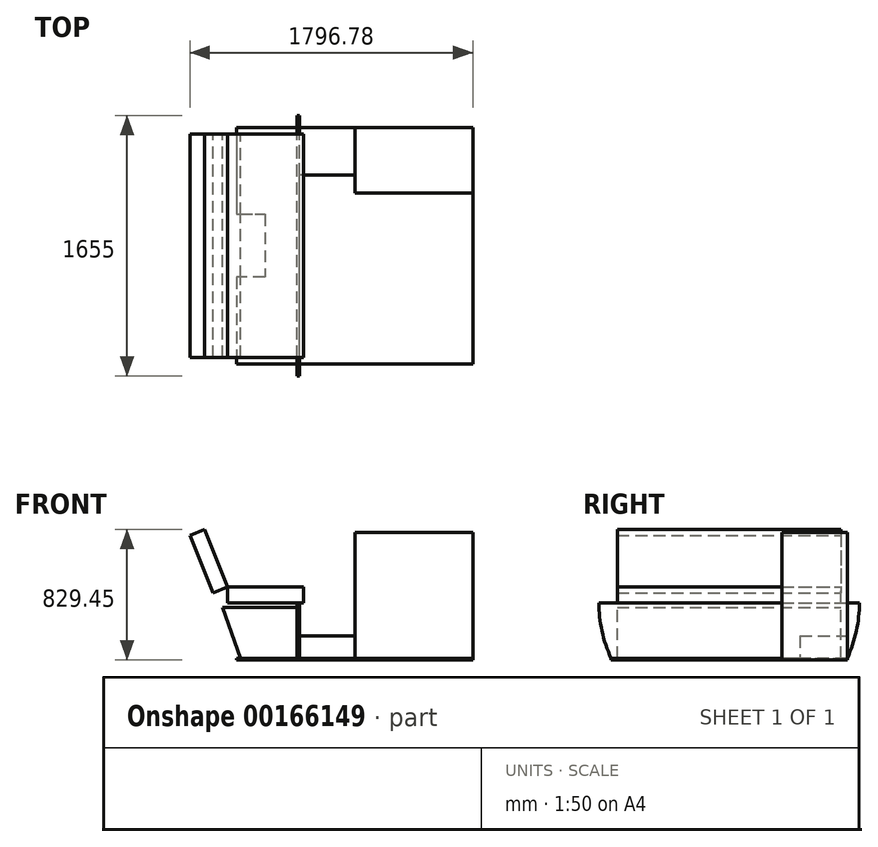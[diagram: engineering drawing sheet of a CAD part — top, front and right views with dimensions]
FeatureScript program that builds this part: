
annotation { "Feature Type Name" : "Feature", "Feature Type Description" : "" }
export const myFeature = defineFeature(function(context is Context, id is Id, definition is map)
    precondition{}
    {
        {
            var Q0;
            Q0=qCreatedBy(makeId("Top.planeOp"),FACE);
            var sketch = newSketch(context, id + "F0", { "sketchPlane" : qUnion([Q0])});
            skLineSegment(sketch, "E0.bottom", {"start": v(750, 750) * mm, "end": v(-750, 750) * mm});
            skLineSegment(sketch, "E0.top", {"start": v(750, -750) * mm, "end": v(-750, -750) * mm});
            skLineSegment(sketch, "E0.left", {"start": v(750, 750) * mm, "end": v(750, -750) * mm});
            skLineSegment(sketch, "E0.right", {"start": v(-750, 750) * mm, "end": v(-750, 200) * mm});
            skPoint(sketch, "E0.middle", {"position": v(0, 0) * mm});
            skLineSegment(sketch, "E1", {"start": v(-750, 200) * mm, "end": v(-570, 200) * mm});
            skLineSegment(sketch, "E2", {"start": v(-570, 200) * mm, "end": v(-570, -200) * mm});
            skLineSegment(sketch, "E3", {"start": v(-570, -200) * mm, "end": v(-750, -200) * mm});
            skLineSegment(sketch, "E4.trimOffspring", {"start": v(-750, -200) * mm, "end": v(-750, -750) * mm});
            skLineSegment(sketch, "E5", {"start": v(-750, 0) * mm, "end": v(750, 0) * mm, "construction": true});
            skSolve(sketch);
        }
        {
            var Q0;
            Q0=makeQuery(id+"F0.imprint","IMPRINT",FACE,{"disambiguationData":[TD([[makeQuery(id+"F0.imprint","IMPRINT",EDGE,{"derivedFrom":sQuery(id+"F0.wireOp",EDGE,"E0.bottom")}),1.0]])]});
            extrude(context, id + "F1", {"entities" : qUnion([Q0]), "depth" : 12 * mm});
        }
        {
            var Q0;
            Q0=makeQuery(id+"F1.opExtrude","CAP_FACE",FACE,{"disambiguationData":[OSD([sQuery(id+"F0.wireOp",EDGE,"E0.bottom"),sQuery(id+"F0.wireOp",EDGE,"E0.top"),sQuery(id+"F0.wireOp",EDGE,"E0.left"),sQuery(id+"F0.wireOp",EDGE,"E0.right"),sQuery(id+"F0.wireOp",EDGE,"E1"),sQuery(id+"F0.wireOp",EDGE,"E2"),sQuery(id+"F0.wireOp",EDGE,"E3"),sQuery(id+"F0.wireOp",EDGE,"E4.trimOffspring")])],"isStart":false});
            var sketch = newSketch(context, id + "F2", { "sketchPlane" : qUnion([Q0])});
            skLineSegment(sketch, "E6", {"start": v(-350, 750) * mm, "end": v(-350, -750) * mm, "construction": true});
            skLineSegment(sketch, "E7", {"start": v(0, 750) * mm, "end": v(0, 335) * mm, "construction": true});
            skLineSegment(sketch, "E8", {"start": v(0, 335) * mm, "end": v(750, 335) * mm, "construction": true});
            skLineSegment(sketch, "E9", {"start": v(-350, 450) * mm, "end": v(0, 450) * mm, "construction": true});
            skLineSegment(sketch, "E10", {"start": v(-366, 750) * mm, "end": v(-366, -750) * mm});
            skLineSegment(sketch, "E11", {"start": v(16, 466) * mm, "end": v(-366, 466) * mm});
            skLineSegment(sketch, "E12", {"start": v(16, 466) * mm, "end": v(16, 351) * mm});
            skLineSegment(sketch, "E13", {"start": v(750, 351) * mm, "end": v(16, 351) * mm});
            skLineSegment(sketch, "E14", {"start": v(-350, -750) * mm, "end": v(-350, -770) * mm});
            skLineSegment(sketch, "E15", {"start": v(-350, -770) * mm, "end": v(750, -770) * mm});
            skLineSegment(sketch, "E16", {"start": v(750, -770) * mm, "end": v(750, -750) * mm});
            skLineSegment(sketch, "E17.bottom", {"start": v(-350, -705) * mm, "end": v(750, -705) * mm});
            skLineSegment(sketch, "E17.top", {"start": v(-350, -670) * mm, "end": v(750, -670) * mm});
            skLineSegment(sketch, "E17.left", {"start": v(-350, -705) * mm, "end": v(-350, -670) * mm});
            skLineSegment(sketch, "E17.right", {"start": v(750, -705) * mm, "end": v(750, -670) * mm});
            skLineSegment(sketch, "E18", {"start": v(-350, -710) * mm, "end": v(750, -710) * mm});
            skLineSegment(sketch, "E19", {"start": v(750, -710) * mm, "end": v(750, -750) * mm});
            skLineSegment(sketch, "E20", {"start": v(-350, -710) * mm, "end": v(-350, -750) * mm});
            skLineSegment(sketch, "E21.bottom", {"start": v(-350, 450) * mm, "end": v(0, 450) * mm});
            skLineSegment(sketch, "E21.top", {"start": v(-350, 415) * mm, "end": v(0, 415) * mm});
            skLineSegment(sketch, "E21.left", {"start": v(-350, 450) * mm, "end": v(-350, 415) * mm});
            skLineSegment(sketch, "E21.right", {"start": v(0, 450) * mm, "end": v(0, 415) * mm});
            skLineSegment(sketch, "E22.bottom", {"start": v(-350, 410) * mm, "end": v(0, 410) * mm});
            skLineSegment(sketch, "E22.top", {"start": v(-350, 375) * mm, "end": v(0, 375) * mm});
            skLineSegment(sketch, "E22.left", {"start": v(-350, 410) * mm, "end": v(-350, 375) * mm});
            skLineSegment(sketch, "E22.right", {"start": v(0, 410) * mm, "end": v(0, 375) * mm});
            skLineSegment(sketch, "E23.bottom", {"start": v(-350, 370) * mm, "end": v(0, 370) * mm});
            skLineSegment(sketch, "E23.top", {"start": v(-350, 335) * mm, "end": v(0, 335) * mm});
            skLineSegment(sketch, "E23.left", {"start": v(-350, 370) * mm, "end": v(-350, 335) * mm});
            skLineSegment(sketch, "E23.right", {"start": v(0, 370) * mm, "end": v(0, 335) * mm});
            skLineSegment(sketch, "E24", {"start": v(-350, 450) * mm, "end": v(-350, -705) * mm});
            skLineSegment(sketch, "E25", {"start": v(0, 450) * mm, "end": v(0, 335) * mm});
            skLineSegment(sketch, "E26", {"start": v(0, 335) * mm, "end": v(750, 335) * mm});
            skSolve(sketch);
        }
        {
            var Q0;
            Q0=makeQuery(id+"F1.opExtrude","CAP_FACE",FACE,{"disambiguationData":[OSD([sQuery(id+"F0.wireOp",EDGE,"E0.bottom"),sQuery(id+"F0.wireOp",EDGE,"E0.top"),sQuery(id+"F0.wireOp",EDGE,"E0.left"),sQuery(id+"F0.wireOp",EDGE,"E0.right"),sQuery(id+"F0.wireOp",EDGE,"E1"),sQuery(id+"F0.wireOp",EDGE,"E2"),sQuery(id+"F0.wireOp",EDGE,"E3"),sQuery(id+"F0.wireOp",EDGE,"E4.trimOffspring")])],"isStart":false});
            var sketch = newSketch(context, id + "F3", { "sketchPlane" : qUnion([Q0])});
            skLineSegment(sketch, "E27.bottom", {"start": v(750, 750) * mm, "end": v(0, 750) * mm});
            skLineSegment(sketch, "E27.top", {"start": v(750, 335) * mm, "end": v(0, 335) * mm});
            skLineSegment(sketch, "E27.left", {"start": v(750, 750) * mm, "end": v(750, 335) * mm});
            skLineSegment(sketch, "E27.right", {"start": v(0, 750) * mm, "end": v(0, 335) * mm});
            skLineSegment(sketch, "E28", {"start": v(0, 450) * mm, "end": v(-350, 450) * mm});
            skLineSegment(sketch, "E29", {"start": v(-350, 450) * mm, "end": v(-350, 750) * mm});
            skSolve(sketch);
        }
        {
            var Q0;
            Q0=sQuery(id+"F3.wireOp",EDGE,"E28");
            var Q1;
            Q1=sQuery(id+"F3.wireOp",VERTEX,"E28.end");
            cPlane(context, id + "F4", {"entities" : qUnion([Q0, Q1]), "cplaneType" : CPlaneType.LINE_POINT, "offset" : 25 * mm, "width" : 150 * mm, "height" : 150 * mm});
        }
        {
            var Q0;
            Q0=qCreatedBy(id+"F4.planeOp",FACE);
            var sketch = newSketch(context, id + "F5", { "sketchPlane" : qUnion([Q0])});
            skLineSegment(sketch, "E30", {"start": v(827.5, 364) * mm, "end": v(-827.5, 364) * mm});
            skArc(sketch, "E31", {"start": v(750, 12) * mm, "mid": v(807.9, 183.78) * mm, "end": v(827.5, 364) * mm});
            skLineSegment(sketch, "E32", {"start": v(827.5, 72.78) * mm, "end": v(827.5, 364) * mm, "construction": true});
            skArc(sketch, "E33.MirrorCS", {"start": v(-750, 12) * mm, "mid": v(-807.9, 183.78) * mm, "end": v(-827.5, 364) * mm});
            skLineSegment(sketch, "E34", {"start": v(750, 12) * mm, "end": v(-750, 12) * mm});
            skSolve(sketch);
        }
        {
            var Q0;
            Q0=makeQuery(id+"F5.imprint","IMPRINT",FACE,{"disambiguationData":[TD([[makeQuery(id+"F5.imprint","IMPRINT",EDGE,{"derivedFrom":sQuery(id+"F5.wireOp",EDGE,"E30")}),1.0]])]});
            extrude(context, id + "F6", {"entities" : qUnion([Q0]), "operationType" : NewBodyOperationType.ADD, "depth" : 18 * mm});
        }
        {
            var Q0;
            {var subQ1=sQuery(id+"F3.wireOp",EDGE,"E27.bottom");Q0=makeQuery(id+"F3.imprint","IMPRINT",FACE,{"disambiguationData":[TD([[makeQuery(id+"F3.imprint","IMPRINT",EDGE,{"derivedFrom":subQ1}),1.0]])]});}
            extrude(context, id + "F7", {"entities" : qUnion([Q0]), "operationType" : NewBodyOperationType.ADD, "depth" : 800 * mm});
        }
        {
            var Q0;
            {var subQ3=sQuery(id+"F3.wireOp",EDGE,"E28");Q0=makeQuery(id+"F3.imprint","IMPRINT",FACE,{"disambiguationData":[TD([[makeQuery(id+"F3.imprint","IMPRINT",EDGE,{"derivedFrom":subQ3}),-1.0]])]});}
            extrude(context, id + "F8", {"entities" : qUnion([Q0]), "operationType" : NewBodyOperationType.ADD, "depth" : 140 * mm});
        }
        {
            var Q0;
            Q0=qCreatedBy(makeId("Front.planeOp"),FACE);
            var sketch = newSketch(context, id + "F9", { "sketchPlane" : qUnion([Q0])});
            skLineSegment(sketch, "E35.bottom", {"start": v(-324.6, 364) * mm, "end": v(-808.33, 364) * mm});
            skLineSegment(sketch, "E35.top", {"start": v(-324.6, 464) * mm, "end": v(-808.33, 464) * mm});
            skLineSegment(sketch, "E35.left", {"start": v(-324.6, 364) * mm, "end": v(-324.6, 464) * mm});
            skLineSegment(sketch, "E35.right", {"start": v(-808.33, 364) * mm, "end": v(-808.33, 464) * mm});
            skLineSegment(sketch, "E36", {"start": v(-839.36, 333.23) * mm, "end": v(-725.7, 12) * mm});
            skLineSegment(sketch, "E37", {"start": v(-725.7, 12) * mm, "end": v(-368, 12) * mm});
            skLineSegment(sketch, "E38", {"start": v(-368, 12) * mm, "end": v(-368, 364) * mm});
            skLineSegment(sketch, "E39.bottom", {"start": v(-953.88, 829.45) * mm, "end": v(-808.33, 464) * mm});
            skLineSegment(sketch, "E39.top", {"start": v(-1046.78, 792.45) * mm, "end": v(-901.23, 427) * mm});
            skLineSegment(sketch, "E39.left", {"start": v(-953.88, 829.45) * mm, "end": v(-1046.78, 792.45) * mm});
            skLineSegment(sketch, "E39.right", {"start": v(-808.33, 464) * mm, "end": v(-901.23, 427) * mm});
            skLineSegment(sketch, "E40", {"start": v(-839.36, 333.23) * mm, "end": v(-368, 333.23) * mm});
            skSolve(sketch);
        }
        {
            var Q0;
            Q0=makeQuery(id+"F9.imprint","IMPRINT",FACE,{"disambiguationData":[TD([[makeQuery(id+"F9.imprint","IMPRINT",EDGE,{"derivedFrom":sQuery(id+"F9.wireOp",EDGE,"E39.bottom")}),-1.0]])]});
            var Q1;
            Q1=makeQuery(id+"F9.imprint","IMPRINT",FACE,{"disambiguationData":[TD([[makeQuery(id+"F9.imprint","IMPRINT",EDGE,{"derivedFrom":sQuery(id+"F9.wireOp",EDGE,"E35.top")}),1.0]])]});
            var Q2;
            Q2=makeQuery(id+"F9.imprint","IMPRINT",FACE,{"disambiguationData":[TD([[makeQuery(id+"F9.imprint","IMPRINT",EDGE,{"derivedFrom":sQuery(id+"F9.wireOp",EDGE,"E36")}),1.0]])]});
            extrude(context, id + "F10", {"entities" : qUnion([Q0, Q1, Q2]), "operationType" : NewBodyOperationType.ADD, "endBound" : BoundingType.SYMMETRIC, "depth" : 1420 * mm});
        }
    });
